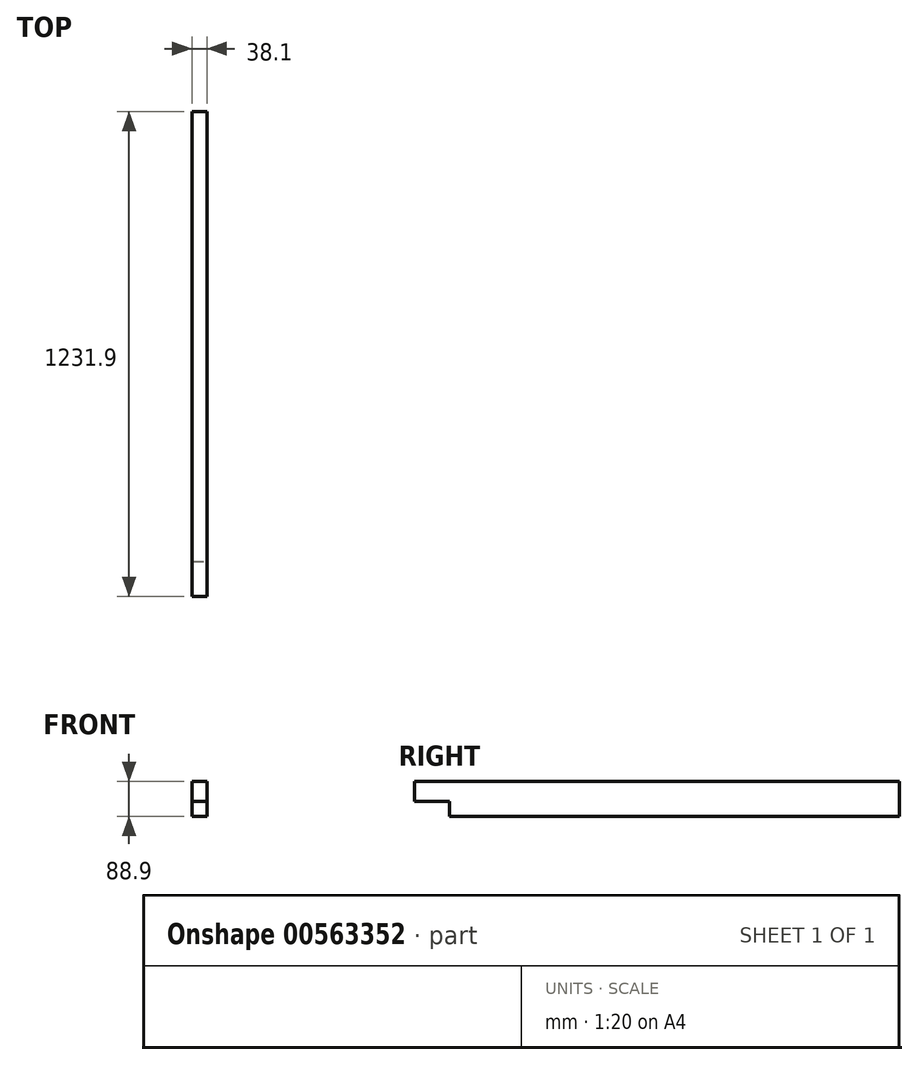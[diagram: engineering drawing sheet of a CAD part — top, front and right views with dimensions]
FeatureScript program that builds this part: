
annotation { "Feature Type Name" : "Feature", "Feature Type Description" : "" }
export const myFeature = defineFeature(function(context is Context, id is Id, definition is map)
    precondition{}
    {
        {
            var Q0;
            Q0=qCreatedBy(makeId("Top.planeOp"),FACE);
            var sketch = newSketch(context, id + "F0", { "sketchPlane" : qUnion([Q0])});
            skLineSegment(sketch, "E0.bottom", {"start": v(19.05, -615.95) * mm, "end": v(-19.05, -615.95) * mm});
            skLineSegment(sketch, "E0.top", {"start": v(19.05, 615.95) * mm, "end": v(-19.05, 615.95) * mm});
            skLineSegment(sketch, "E0.left", {"start": v(19.05, -615.95) * mm, "end": v(19.05, 615.95) * mm});
            skLineSegment(sketch, "E0.right", {"start": v(-19.05, -615.95) * mm, "end": v(-19.05, 615.95) * mm});
            skPoint(sketch, "E0.middle", {"position": v(0, 0) * mm});
            skLineSegment(sketch, "E1", {"start": v(-19.05, -527.05) * mm, "end": v(19.05, -527.05) * mm});
            skSolve(sketch);
        }
        {
            var Q0;
            {var subQ0=sQuery(id+"F0.wireOp",EDGE,"E0.top");Q0=makeQuery(id+"F0.imprint","IMPRINT",FACE,{"disambiguationData":[TD([[makeQuery(id+"F0.imprint","IMPRINT",EDGE,{"derivedFrom":subQ0}),1.0]])]});}
            extrude(context, id + "F1", {"entities" : qUnion([Q0]), "oppositeDirection" : true, "depth" : 88.9 * mm, "offsetDistance" : 25.4 * mm});
        }
        {
            var Q0;
            {var subQ0=sQuery(id+"F0.wireOp",EDGE,"E0.bottom");Q0=makeQuery(id+"F0.imprint","IMPRINT",FACE,{"disambiguationData":[TD([[makeQuery(id+"F0.imprint","IMPRINT",EDGE,{"derivedFrom":subQ0}),-1.0]])]});}
            extrude(context, id + "F2", {"entities" : qUnion([Q0]), "operationType" : NewBodyOperationType.ADD, "oppositeDirection" : true, "depth" : 50.8 * mm, "offsetDistance" : 25.4 * mm});
        }
    });
